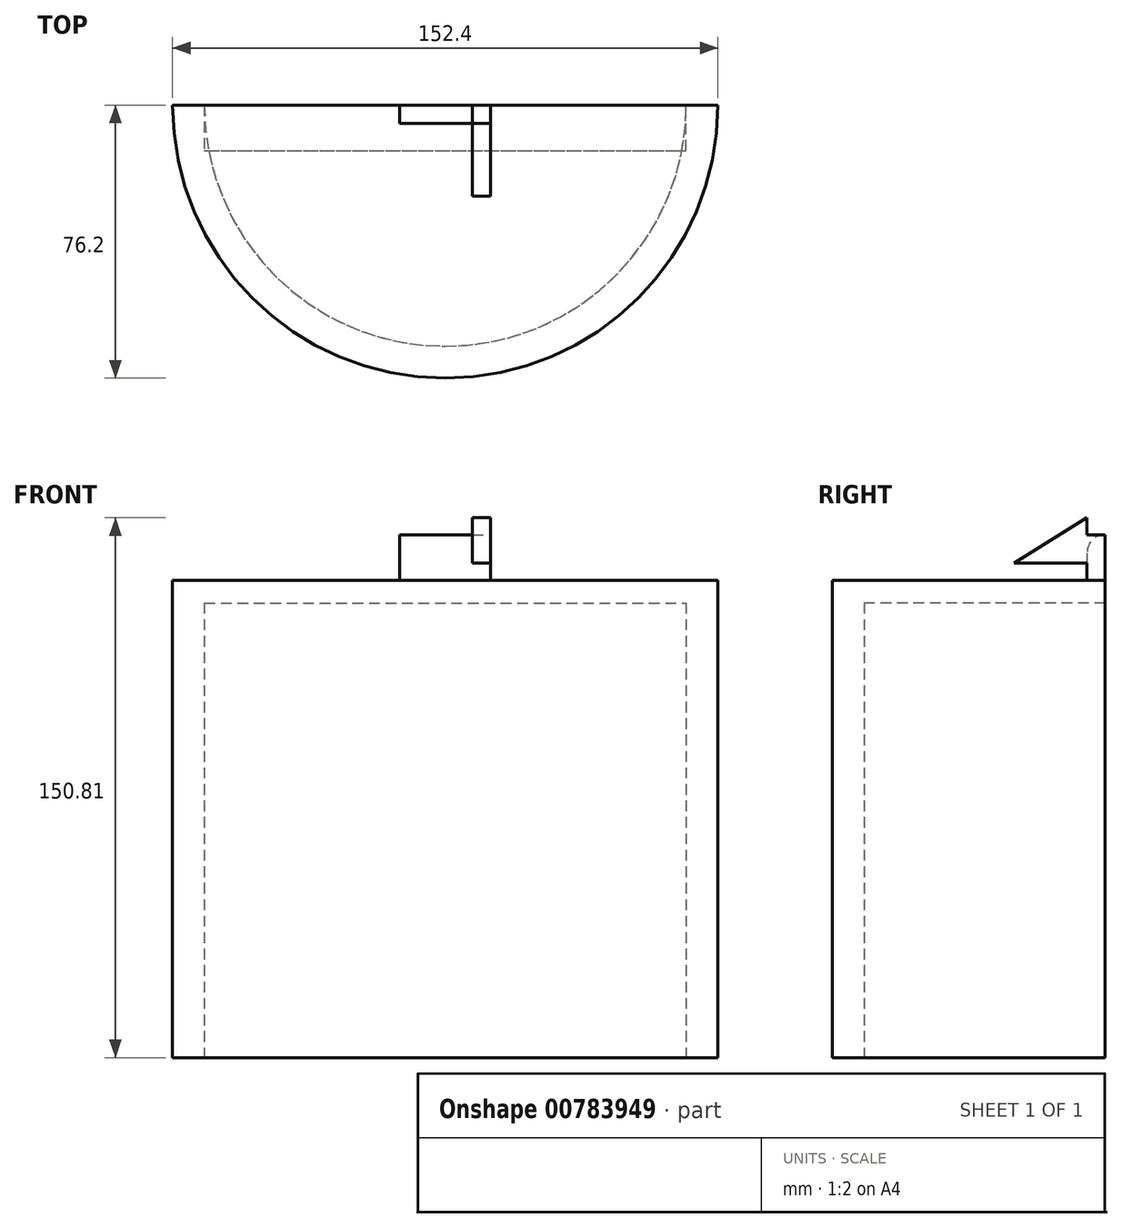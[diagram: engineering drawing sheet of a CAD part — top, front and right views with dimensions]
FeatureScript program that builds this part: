
annotation { "Feature Type Name" : "Feature", "Feature Type Description" : "" }
export const myFeature = defineFeature(function(context is Context, id is Id, definition is map)
    precondition{}
    {
        {
            var Q0;
            Q0=qCreatedBy(makeId("Top.planeOp"),FACE);
            var sketch = newSketch(context, id + "F0", { "sketchPlane" : qUnion([Q0])});
            skArc(sketch, "E0", {"start": v(76.2, 0) * mm, "mid": v(0, -76.2) * mm, "end": v(-76.2, 0) * mm});
            skLineSegment(sketch, "E1", {"start": v(-67.31, 0) * mm, "end": v(-67.31, -12.7) * mm});
            skLineSegment(sketch, "E2", {"start": v(-67.31, -12.7) * mm, "end": v(67.31, -12.7) * mm});
            skLineSegment(sketch, "E3", {"start": v(67.31, -12.7) * mm, "end": v(67.31, 0) * mm});
            skLineSegment(sketch, "E4", {"start": v(67.31, 0) * mm, "end": v(76.2, 0) * mm});
            skLineSegment(sketch, "E5", {"start": v(-76.2, 0) * mm, "end": v(-67.31, 0) * mm});
            skSolve(sketch);
        }
        {
            var Q0;
            Q0 = qSketchRegion(id + "F0", true);
            extrude(context, id + "F1", {"entities" : qUnion([Q0]), "depth" : 3 / 406.4 * mm, "offsetDistance" : 25.4 * mm});
        }
        {
            var Q0;
            Q0=makeQuery(id+"F1.opExtrude","CAP_FACE",FACE,{"disambiguationData":[OSD([sQuery(id+"F0.wireOp",EDGE,"E0"),sQuery(id+"F0.wireOp",EDGE,"E1"),sQuery(id+"F0.wireOp",EDGE,"E2"),sQuery(id+"F0.wireOp",EDGE,"E3"),sQuery(id+"F0.wireOp",EDGE,"E4"),sQuery(id+"F0.wireOp",EDGE,"E5")])],"isStart":false});
            var sketch = newSketch(context, id + "F2", { "sketchPlane" : qUnion([Q0])});
            skArc(sketch, "E6", {"start": v(-76.2, 0) * mm, "mid": v(0, -76.2) * mm, "end": v(76.2, 0) * mm});
            skArc(sketch, "E7", {"start": v(-67.31, 0) * mm, "mid": v(0, -67.31) * mm, "end": v(67.31, 0) * mm});
            skLineSegment(sketch, "E8", {"start": v(-67.31, 0) * mm, "end": v(-76.2, 0) * mm});
            skLineSegment(sketch, "E9", {"start": v(67.31, 0) * mm, "end": v(76.2, 0) * mm});
            skSolve(sketch);
        }
        {
            var Q0;
            Q0 = qSketchRegion(id + "F2", true);
            extrude(context, id + "F3", {"entities" : qUnion([Q0]), "operationType" : NewBodyOperationType.ADD, "depth" : 127 * mm, "offsetDistance" : 25.4 * mm});
        }
        {
            var Q0;
            Q0=makeQuery(id+"F3.opExtrude","CAP_FACE",FACE,{"disambiguationData":[OSD([sQuery(id+"F2.wireOp",EDGE,"E6"),sQuery(id+"F2.wireOp",EDGE,"E7"),sQuery(id+"F2.wireOp",EDGE,"E8"),sQuery(id+"F2.wireOp",EDGE,"E9")])],"isStart":false});
            var sketch = newSketch(context, id + "F4", { "sketchPlane" : qUnion([Q0])});
            skArc(sketch, "E10", {"start": v(-76.2, 0) * mm, "mid": v(0, -76.2) * mm, "end": v(76.2, 0) * mm});
            skLineSegment(sketch, "E11", {"start": v(-76.2, 0) * mm, "end": v(76.2, 0) * mm});
            skSolve(sketch);
        }
        {
            var Q0;
            Q0 = qSketchRegion(id + "F4", true);
            extrude(context, id + "F5", {"entities" : qUnion([Q0]), "operationType" : NewBodyOperationType.ADD, "depth" : 6.35 * mm, "offsetDistance" : 25.4 * mm});
        }
        {
            var Q0;
            Q0=makeQuery(id+"F5.opExtrude","CAP_FACE",FACE,{"disambiguationData":[OSD([sQuery(id+"F4.wireOp",EDGE,"E10"),sQuery(id+"F4.wireOp",EDGE,"E11")])],"isStart":false});
            var sketch = newSketch(context, id + "F6", { "sketchPlane" : qUnion([Q0])});
            skLineSegment(sketch, "E12", {"start": v(0, 0) * mm, "end": v(-12.7, 0) * mm});
            skLineSegment(sketch, "E13", {"start": v(-12.7, 0) * mm, "end": v(-12.7, -5.08) * mm});
            skLineSegment(sketch, "E14", {"start": v(0, -5.08) * mm, "end": v(-12.7, -5.08) * mm});
            skLineSegment(sketch, "E15.MirrorCS", {"start": v(12.7, 0) * mm, "end": v(12.7, -5.08) * mm});
            skLineSegment(sketch, "E16.MirrorCS", {"start": v(0, 0) * mm, "end": v(12.7, 0) * mm});
            skLineSegment(sketch, "E17.MirrorCS", {"start": v(0, -5.08) * mm, "end": v(12.7, -5.08) * mm});
            skSolve(sketch);
        }
        {
            var Q0;
            Q0 = qSketchRegion(id + "F6", true);
            extrude(context, id + "F7", {"entities" : qUnion([Q0]), "operationType" : NewBodyOperationType.ADD, "depth" : 12.7 * mm, "offsetDistance" : 25.4 * mm});
        }
        {
            var Q0;
            Q0=makeQuery(id+"F7.opExtrude","SWEPT_FACE",FACE,{"disambiguationData":[OSD([sQuery(id+"F6.wireOp",EDGE,"E15.MirrorCS")])]});
            var sketch = newSketch(context, id + "F8", { "sketchPlane" : qUnion([Q0])});
            skLineSegment(sketch, "E18", {"start": v(0, 138.11) * mm, "end": v(-25.4, 138.11) * mm, "construction": true});
            skLineSegment(sketch, "E19", {"start": v(-25.4, 138.11) * mm, "end": v(-5.08, 138.11) * mm});
            skLineSegment(sketch, "E20", {"start": v(-5.08, 138.11) * mm, "end": v(-5.08, 150.81) * mm});
            skLineSegment(sketch, "E21", {"start": v(-5.08, 150.81) * mm, "end": v(-25.4, 138.11) * mm});
            skSolve(sketch);
        }
        {
            var Q0;
            Q0 = qSketchRegion(id + "F8", true);
            extrude(context, id + "F9", {"entities" : qUnion([Q0]), "operationType" : NewBodyOperationType.ADD, "oppositeDirection" : true, "depth" : 5.08 * mm, "offsetDistance" : 25.4 * mm});
        }
        {
            var Q0;
            Q0=makeQuery(id+"Faw6R903dyJn3Pk_1.1.F9.boolean.opBoolean","MERGE",EDGE,{"derivedFrom":[makeQuery(id+"F9.boolean.opBoolean","SPLIT",EDGE,{"derivedFrom":makeQuery(id+"F7.opExtrude","CAP_EDGE",EDGE,{"disambiguationData":[OSD([sQuery(id+"F6.wireOp",EDGE,"E14"),sQuery(id+"F6.wireOp",EDGE,"E17.MirrorCS")])],"isStart":false})}),makeQuery(id+"Faw6R903dyJn3Pk_1.1.F9.opExtrude","SWEPT_EDGE",EDGE,{"disambiguationData":[OSD([sQuery(id+"F6.wireOp",EDGE,"E15.MirrorCS"),sQuery(id+"F8.wireOp",EDGE,"E20"),sQuery(id+"F8.wireOp",EDGE,"E21")])]})]});
            fillet(context, id + "F10", {"entities" : qUnion([Q0]), "radius" : 5.08 * mm, "tangentPropagation" : true, "allowEdgeOverflow" : false});
        }
    });
